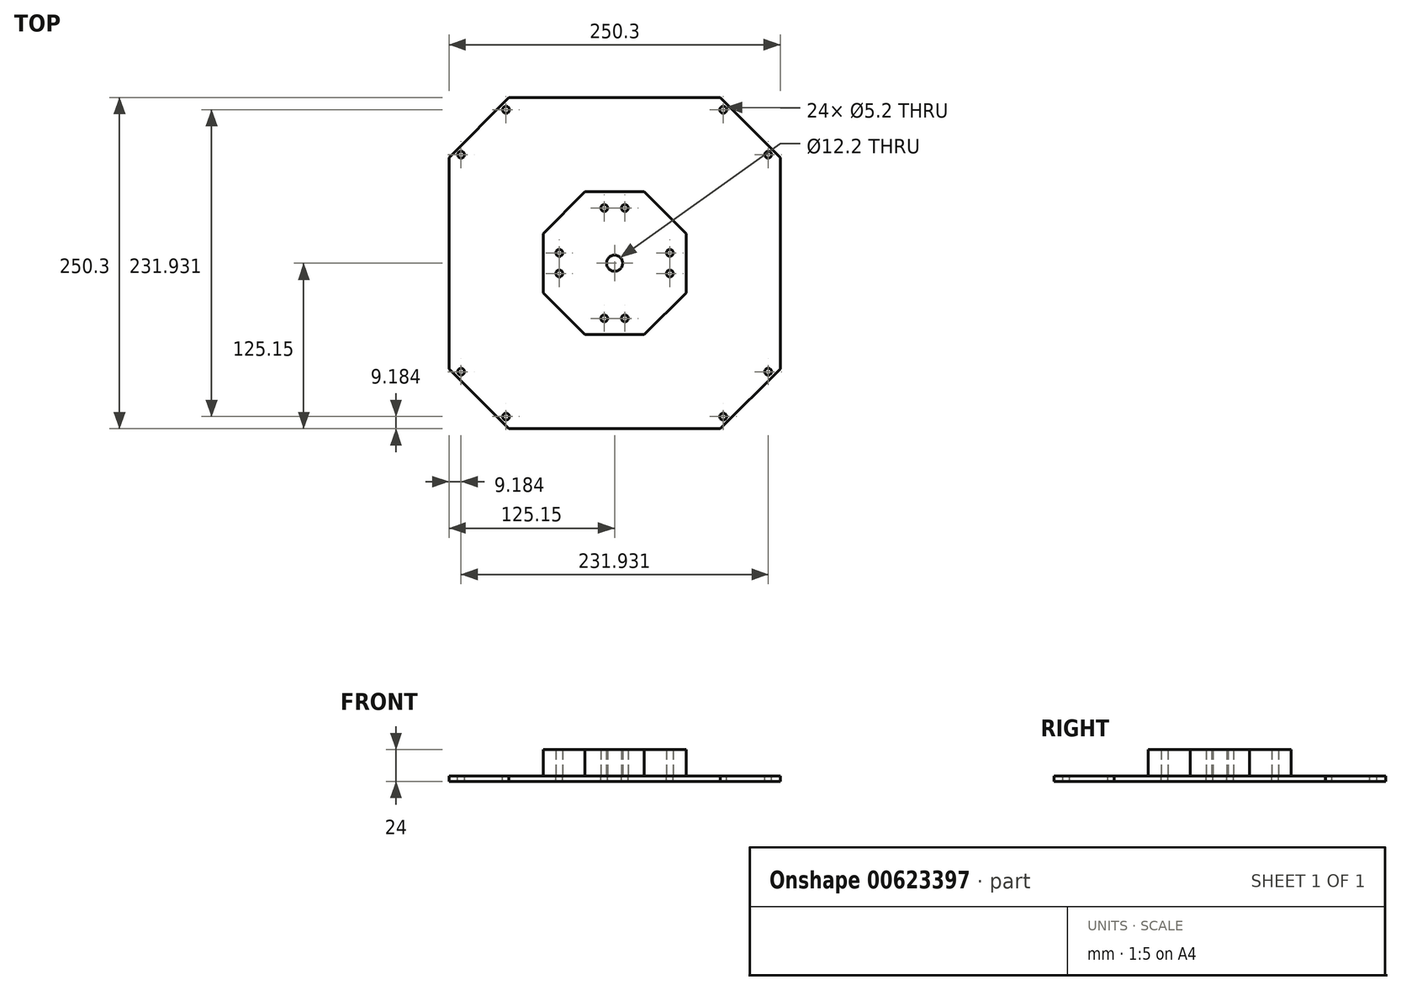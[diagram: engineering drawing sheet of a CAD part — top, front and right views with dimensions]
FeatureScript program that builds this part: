
annotation { "Feature Type Name" : "Feature", "Feature Type Description" : "" }
export const myFeature = defineFeature(function(context is Context, id is Id, definition is map)
    precondition{}
    {
        {
            var Q0;
            Q0=qCreatedBy(makeId("Top.planeOp"),FACE);
            var sketch = newSketch(context, id + "F0", { "sketchPlane" : qUnion([Q0])});
            skLineSegment(sketch, "E0", {"start": v(-102.53, 102.53) * mm, "end": v(102.53, -102.53) * mm, "construction": true});
            skLineSegment(sketch, "E1", {"start": v(-100.97, -100.97) * mm, "end": v(102.5, 102.5) * mm, "construction": true});
            skLineSegment(sketch, "E2", {"start": v(0, 0) * mm, "end": v(0, 125.15) * mm, "construction": true});
            skLineSegment(sketch, "E3", {"start": v(102.5, 102.5) * mm, "end": v(79.85, 125.15) * mm});
            skLineSegment(sketch, "E4", {"start": v(79.85, 125.15) * mm, "end": v(-79.91, 125.15) * mm});
            skLineSegment(sketch, "E5", {"start": v(-79.91, 125.15) * mm, "end": v(-102.53, 102.53) * mm});
            skLineSegment(sketch, "E6.MirrorCS", {"start": v(102.5, 102.5) * mm, "end": v(125.15, 79.85) * mm});
            skLineSegment(sketch, "E7.MirrorCS", {"start": v(125.15, 79.85) * mm, "end": v(125.15, -79.91) * mm});
            skLineSegment(sketch, "E8.MirrorCS", {"start": v(125.15, -79.91) * mm, "end": v(102.53, -102.53) * mm});
            skLineSegment(sketch, "E9.MirrorCS", {"start": v(-125.15, 79.91) * mm, "end": v(-102.53, 102.53) * mm});
            skLineSegment(sketch, "E10.MirrorCS", {"start": v(-125.15, -79.85) * mm, "end": v(-125.15, 79.91) * mm});
            skLineSegment(sketch, "E11.MirrorCS", {"start": v(-102.5, -102.5) * mm, "end": v(-125.15, -79.85) * mm});
            skLineSegment(sketch, "E12.MirrorCS", {"start": v(-102.5, -102.5) * mm, "end": v(-79.85, -125.15) * mm});
            skLineSegment(sketch, "E13.MirrorCS", {"start": v(-79.85, -125.15) * mm, "end": v(79.91, -125.15) * mm});
            skLineSegment(sketch, "E14.MirrorCS", {"start": v(79.91, -125.15) * mm, "end": v(102.53, -102.53) * mm});
            skSolve(sketch);
        }
        {
            var Q0;
            Q0=makeQuery(id+"F0.imprint","IMPRINT",FACE,{"disambiguationData":[TD([[makeQuery(id+"F0.imprint","IMPRINT",EDGE,{"derivedFrom":sQuery(id+"F0.wireOp",EDGE,"wkNUffIB-qnCA-ifZx-wQDp-ZMm1OhZD6AcE")}),-1.0]])]});
            var Q1;
            Q1=makeQuery(id+"F0.imprint","IMPRINT",FACE,{"disambiguationData":[TD([[makeQuery(id+"F0.imprint","IMPRINT",EDGE,{"derivedFrom":sQuery(id+"F0.wireOp",EDGE,"E3")}),1.0]])]});
            extrude(context, id + "F1", {"entities" : qUnion([Q0, Q1]), "depth" : 4 * mm});
        }
        {
            var Q0;
            Q0=makeQuery(id+"F1.opExtrude","CAP_FACE",FACE,{"disambiguationData":[OSD([sQuery(id+"F0.wireOp",EDGE,"E3"),sQuery(id+"F0.wireOp",EDGE,"E4"),sQuery(id+"F0.wireOp",EDGE,"E5"),sQuery(id+"F0.wireOp",EDGE,"E6.MirrorCS"),sQuery(id+"F0.wireOp",EDGE,"E7.MirrorCS"),sQuery(id+"F0.wireOp",EDGE,"E8.MirrorCS"),sQuery(id+"F0.wireOp",EDGE,"E9.MirrorCS"),sQuery(id+"F0.wireOp",EDGE,"E10.MirrorCS"),sQuery(id+"F0.wireOp",EDGE,"E11.MirrorCS"),sQuery(id+"F0.wireOp",EDGE,"E12.MirrorCS"),sQuery(id+"F0.wireOp",EDGE,"E13.MirrorCS"),sQuery(id+"F0.wireOp",EDGE,"E14.MirrorCS")])],"isStart":false});
            var sketch = newSketch(context, id + "F2", { "sketchPlane" : qUnion([Q0])});
            skLineSegment(sketch, "E15", {"start": v(0, 0) * mm, "end": v(0, 125.15) * mm, "construction": true});
            skLineSegment(sketch, "E16", {"start": v(0, 0) * mm, "end": v(-125.15, 0) * mm, "construction": true});
            skLineSegment(sketch, "E17", {"start": v(0, 0) * mm, "end": v(-102.53, 102.53) * mm, "construction": true});
            skCircle(sketch, "E18", {"center": v(-7.78, 41.72) * mm, "radius": 2.6 * mm});
            skLineSegment(sketch, "E19", {"start": v(0, 0) * mm, "end": v(-102.5, -102.5) * mm, "construction": true});
            skLineSegment(sketch, "E20.MirrorCS", {"start": v(0, 0) * mm, "end": v(102.53, -102.53) * mm, "construction": true});
            skCircle(sketch, "E21.MirrorC", {"center": v(-41.72, 7.78) * mm, "radius": 2.6 * mm});
            skCircle(sketch, "E22.MirrorC", {"center": v(7.78, -41.72) * mm, "radius": 2.6 * mm});
            skCircle(sketch, "E23.MirrorC", {"center": v(41.72, -7.78) * mm, "radius": 2.6 * mm});
            skCircle(sketch, "E24.1.0", {"center": v(41.72, 7.78) * mm, "radius": 2.6 * mm});
            skCircle(sketch, "E24.1.1", {"center": v(7.78, 41.72) * mm, "radius": 2.6 * mm});
            skCircle(sketch, "E24.1.2", {"center": v(-41.72, -7.78) * mm, "radius": 2.6 * mm});
            skCircle(sketch, "E24.1.3", {"center": v(-7.78, -41.72) * mm, "radius": 2.6 * mm});
            skPoint(sketch, "E24.center", {"position": v(0, 0) * mm});
            skLineSegment(sketch, "E24.anchor1", {"start": v(0, 0) * mm, "end": v(-7.78, 41.72) * mm, "construction": true});
            skLineSegment(sketch, "E24.anchor2", {"start": v(0, 0) * mm, "end": v(41.72, 7.78) * mm, "construction": true});
            skSolve(sketch);
        }
        {
            var Q0;
            Q0=qSketchRegion(id+"F2",true);
            extrude(context, id + "F3", {"entities" : qUnion([Q0]), "operationType" : NewBodyOperationType.REMOVE, "oppositeDirection" : true, "depth" : 20 * mm});
        }
        {
            var Q0;
            Q0=makeQuery(id+"F2.imprint","IMPRINT",FACE,{"disambiguationData":[TD([[makeQuery(id+"F2.imprint","IMPRINT",EDGE,{"derivedFrom":sQuery(id+"F2.wireOp",EDGE,"E18")}),-1.0]])]});
            var sketch = newSketch(context, id + "F4", { "sketchPlane" : qUnion([Q0])});
            skLineSegment(sketch, "E25.0", {"start": v(0, 0) * mm, "end": v(0, 125.15) * mm, "construction": true});
            skLineSegment(sketch, "E25.1", {"start": v(0, 0) * mm, "end": v(-102.53, 102.53) * mm, "construction": true});
            skLineSegment(sketch, "E25.2", {"start": v(0, 0) * mm, "end": v(-125.15, 0) * mm, "construction": true});
            skLineSegment(sketch, "E25.3", {"start": v(0, 0) * mm, "end": v(-102.5, -102.5) * mm, "construction": true});
            skLineSegment(sketch, "E25.4", {"start": v(0, 0) * mm, "end": v(102.53, -102.53) * mm, "construction": true});
            skCircle(sketch, "E26", {"center": v(-82.02, 115.97) * mm, "radius": 2.6 * mm});
            skCircle(sketch, "E27.MirrorC", {"center": v(-115.97, 82.02) * mm, "radius": 2.6 * mm});
            skCircle(sketch, "E28.MirrorC", {"center": v(82.02, -115.97) * mm, "radius": 2.6 * mm});
            skCircle(sketch, "E29.MirrorC", {"center": v(115.97, -82.02) * mm, "radius": 2.6 * mm});
            skCircle(sketch, "E30.1.0", {"center": v(82.02, 115.97) * mm, "radius": 2.6 * mm});
            skCircle(sketch, "E30.1.1", {"center": v(115.97, 82.02) * mm, "radius": 2.6 * mm});
            skCircle(sketch, "E30.1.2", {"center": v(-115.97, -82.02) * mm, "radius": 2.6 * mm});
            skCircle(sketch, "E30.1.3", {"center": v(-82.02, -115.97) * mm, "radius": 2.6 * mm});
            skPoint(sketch, "E30.center", {"position": v(0, 0) * mm});
            skLineSegment(sketch, "E30.anchor1", {"start": v(0, 0) * mm, "end": v(-115.97, 82.02) * mm, "construction": true});
            skLineSegment(sketch, "E30.anchor2", {"start": v(0, 0) * mm, "end": v(82.02, 115.97) * mm, "construction": true});
            skSolve(sketch);
        }
        {
            var Q0;
            Q0=qSketchRegion(id+"F4",true);
            extrude(context, id + "F5", {"entities" : qUnion([Q0]), "operationType" : NewBodyOperationType.REMOVE, "endBound" : BoundingType.THROUGH_ALL, "oppositeDirection" : true, "depth" : 25 * mm});
        }
        {
            var Q0;
            Q0=makeQuery(id+"F1.opExtrude","CAP_FACE",FACE,{"disambiguationData":[OSD([sQuery(id+"F0.wireOp",EDGE,"E3"),sQuery(id+"F0.wireOp",EDGE,"E4"),sQuery(id+"F0.wireOp",EDGE,"E5"),sQuery(id+"F0.wireOp",EDGE,"E6.MirrorCS"),sQuery(id+"F0.wireOp",EDGE,"E7.MirrorCS"),sQuery(id+"F0.wireOp",EDGE,"E8.MirrorCS"),sQuery(id+"F0.wireOp",EDGE,"E9.MirrorCS"),sQuery(id+"F0.wireOp",EDGE,"E10.MirrorCS"),sQuery(id+"F0.wireOp",EDGE,"E11.MirrorCS"),sQuery(id+"F0.wireOp",EDGE,"E12.MirrorCS"),sQuery(id+"F0.wireOp",EDGE,"E13.MirrorCS"),sQuery(id+"F0.wireOp",EDGE,"E14.MirrorCS")])],"isStart":false});
            var sketch = newSketch(context, id + "F6", { "sketchPlane" : qUnion([Q0])});
            skCircle(sketch, "E31.cCircle", {"center": v(0, 0) * mm, "radius": 54 * mm, "construction": true});
            skLineSegment(sketch, "E31.0", {"start": v(-22.37, 54) * mm, "end": v(22.37, 54) * mm});
            skLineSegment(sketch, "E31.1", {"start": v(22.37, 54) * mm, "end": v(54, 22.37) * mm});
            skLineSegment(sketch, "E31.2", {"start": v(54, 22.37) * mm, "end": v(54, -22.37) * mm});
            skLineSegment(sketch, "E31.3", {"start": v(54, -22.37) * mm, "end": v(22.37, -54) * mm});
            skLineSegment(sketch, "E31.4", {"start": v(22.37, -54) * mm, "end": v(-22.37, -54) * mm});
            skLineSegment(sketch, "E31.5", {"start": v(-22.37, -54) * mm, "end": v(-54, -22.37) * mm});
            skLineSegment(sketch, "E31.6", {"start": v(-54, -22.37) * mm, "end": v(-54, 22.37) * mm});
            skLineSegment(sketch, "E31.7", {"start": v(-54, 22.37) * mm, "end": v(-22.37, 54) * mm});
            skPoint(sketch, "E31.0.midPoint", {"position": v(0, 54) * mm});
            skCircle(sketch, "E32", {"center": v(0, 0) * mm, "radius": 6.1 * mm});
            skSolve(sketch);
        }
        {
            var Q0;
            Q0=makeQuery(id+"F6.imprint","IMPRINT",FACE,{"disambiguationData":[TD([[makeQuery(id+"F6.imprint","IMPRINT",EDGE,{"derivedFrom":sQuery(id+"F6.wireOp",EDGE,"E31.0")}),-1.0]])]});
            extrude(context, id + "F7", {"entities" : qUnion([Q0]), "depth" : 20 * mm, "offsetDistance" : 25 * mm});
        }
    });
